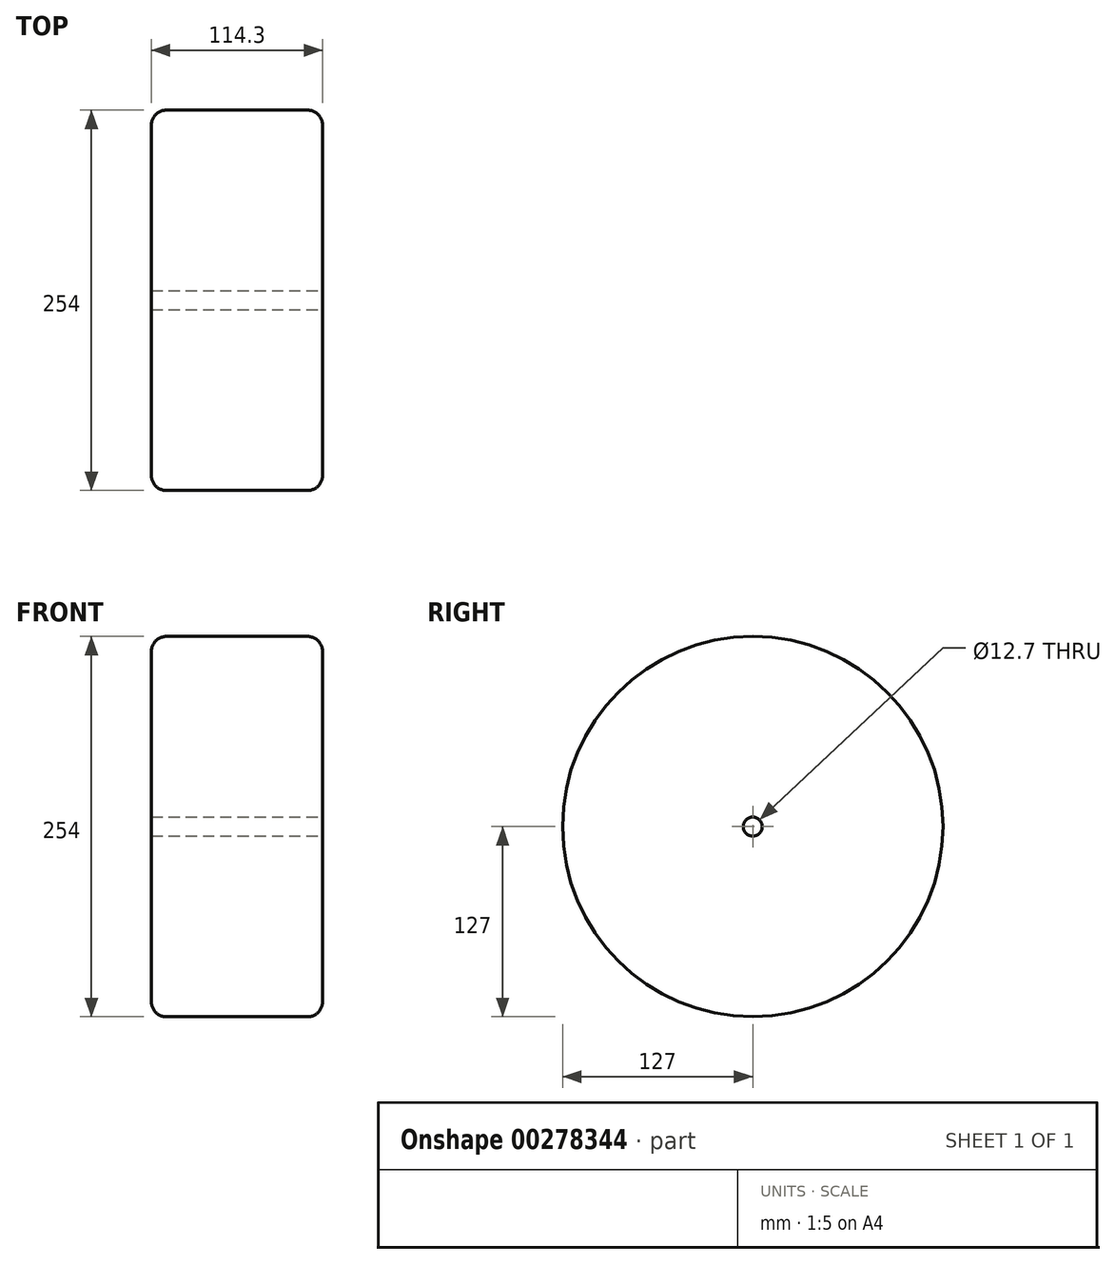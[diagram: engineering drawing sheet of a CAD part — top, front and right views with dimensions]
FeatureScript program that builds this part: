
annotation { "Feature Type Name" : "Feature", "Feature Type Description" : "" }
export const myFeature = defineFeature(function(context is Context, id is Id, definition is map)
    precondition{}
    {
        {
            var Q0;
            Q0=qCreatedBy(makeId("Right.planeOp"),FACE);
            var sketch = newSketch(context, id + "F0", { "sketchPlane" : qUnion([Q0])});
            skCircle(sketch, "E0", {"center": v(0, 0) * mm, "radius": 127 * mm});
            skSolve(sketch);
        }
        {
            var Q0;
            Q0=makeQuery(id+"F0.imprint","IMPRINT",FACE,{"disambiguationData":[TD([[makeQuery(id+"F0.imprint","IMPRINT",EDGE,{"derivedFrom":sQuery(id+"F0.wireOp",EDGE,"E0")}),1.0]])]});
            extrude(context, id + "F1", {"entities" : qUnion([Q0]), "oppositeDirection" : true, "offsetDistance" : 25 * mm, "depth" : 114.3 * mm});
        }
        {
            var Q0;
            Q0=makeQuery(id+"F1.opExtrude","CAP_EDGE",EDGE,{"disambiguationData":[OSD([sQuery(id+"F0.wireOp",EDGE,"E0")])],"isStart":true});
            var Q1;
            Q1=makeQuery(id+"F1.opExtrude","CAP_EDGE",EDGE,{"disambiguationData":[OSD([sQuery(id+"F0.wireOp",EDGE,"E0")])],"isStart":false});
            fillet(context, id + "F2", {"entities" : qUnion([Q0, Q1]), "radius" : 10 * mm, "tangentPropagation" : true, "allowEdgeOverflow" : false});
        }
        {
            var Q0;
            Q0=makeQuery(id+"F1.opExtrude","CAP_FACE",FACE,{"disambiguationData":[OSD([sQuery(id+"F0.wireOp",EDGE,"E0")])],"isStart":true});
            var sketch = newSketch(context, id + "F3", { "sketchPlane" : qUnion([Q0])});
            skCircle(sketch, "E1", {"center": v(0, 0) * mm, "radius": 6.35 * mm});
            skCircle(sketch, "E2", {"center": v(0, 0) * mm, "radius": 63.5 * mm});
            skSolve(sketch);
        }
        {
            var Q0;
            Q0=makeQuery(id+"F3.imprint","IMPRINT",FACE,{"disambiguationData":[TD([[makeQuery(id+"F3.imprint","IMPRINT",EDGE,{"derivedFrom":sQuery(id+"F3.wireOp",EDGE,"E1")}),1.0]])]});
            extrude(context, id + "F4", {"entities" : qUnion([Q0]), "operationType" : NewBodyOperationType.REMOVE, "endBound" : BoundingType.UP_TO_NEXT, "oppositeDirection" : true, "depth" : 25 * mm});
        }
    });
